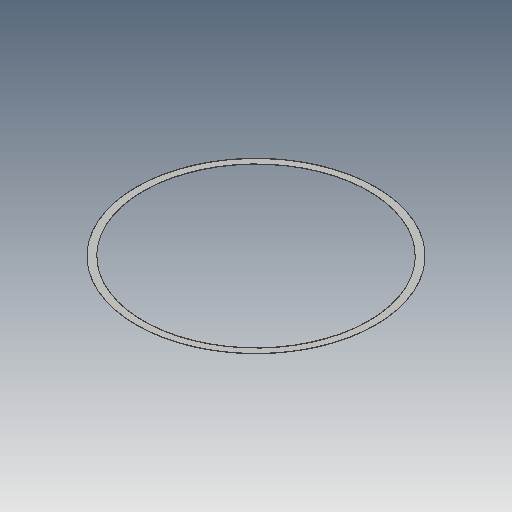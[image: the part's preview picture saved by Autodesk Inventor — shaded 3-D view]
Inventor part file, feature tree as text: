
AUTODESK INVENTOR PART (.ipt)
format: ipt  version: 2019 (Build 230136000, 136)  size: 82,432 bytes
history: native  units: mm
features: extrude x1
ambient origin geometry x8: Origin, YZ Plane, XZ Plane, XY Plane, X Axis, Y Axis, Z Axis, Center Point
bodies: Solid1 (feature_tree)
feature tree (1):
  extrude  "Extrude1"  [1 undecoded]
note: 1 required parameter value undecoded (feature->parameter linkage not recoverable at this tier; creation-order binding heuristic only, values carry confidence <= 0.55)
